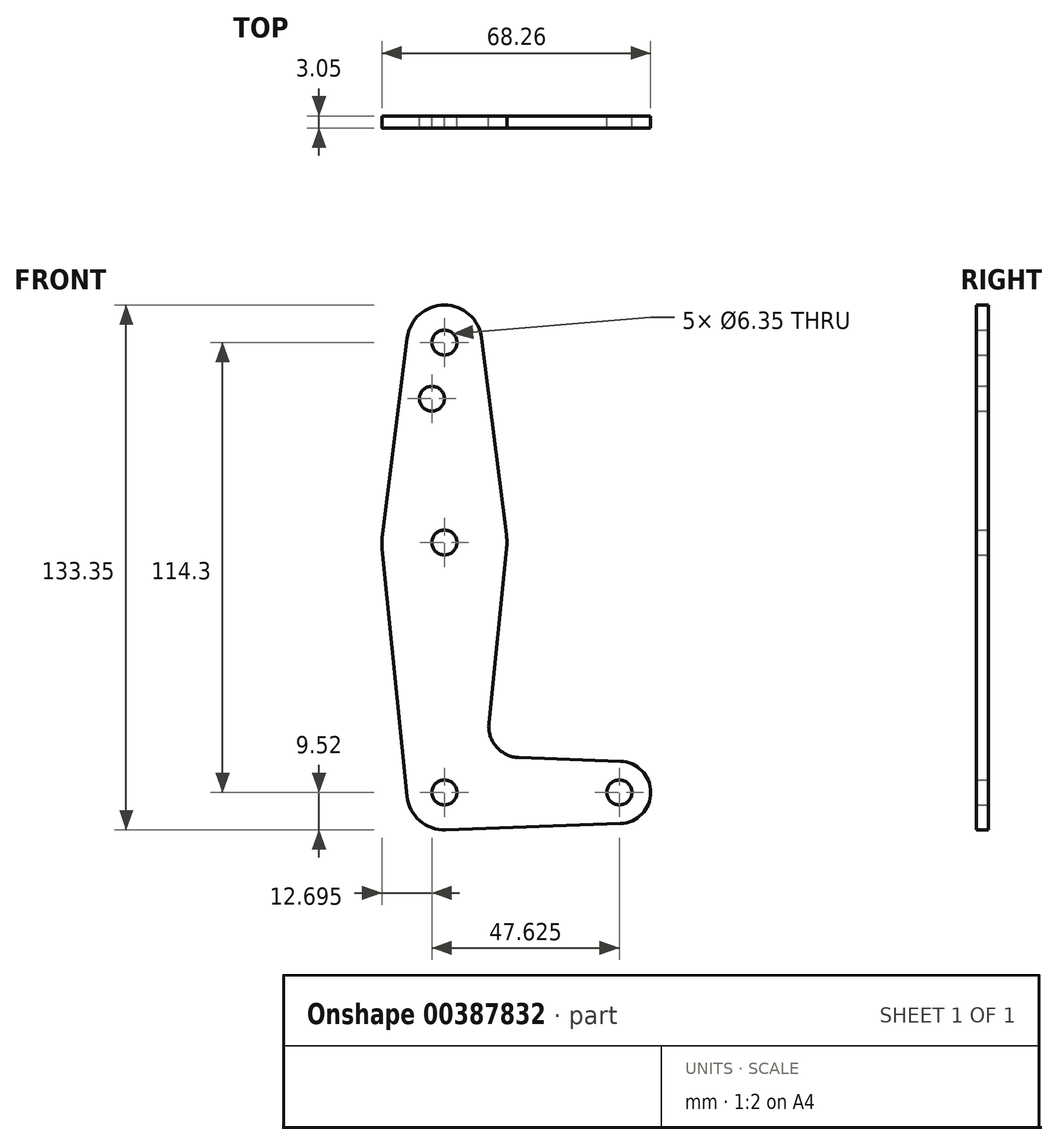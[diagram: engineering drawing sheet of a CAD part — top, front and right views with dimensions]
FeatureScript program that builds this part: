
annotation { "Feature Type Name" : "Feature", "Feature Type Description" : "" }
export const myFeature = defineFeature(function(context is Context, id is Id, definition is map)
    precondition{}
    {
        {
            var Q0;
            Q0=qCreatedBy(makeId("Front.planeOp"),FACE);
            var sketch = newSketch(context, id + "F0", { "sketchPlane" : qUnion([Q0])});
            skLineSegment(sketch, "E0", {"start": v(0, 114.3) * mm, "end": v(0, 0) * mm, "construction": true});
            skLineSegment(sketch, "E1", {"start": v(0, 0) * mm, "end": v(44.45, 0) * mm, "construction": true});
            skCircle(sketch, "E2", {"center": v(0, 114.3) * mm, "radius": 9.53 * mm});
            skCircle(sketch, "E3", {"center": v(0, 63.5) * mm, "radius": 15.88 * mm});
            skCircle(sketch, "E4", {"center": v(44.45, 0) * mm, "radius": 7.94 * mm});
            skLineSegment(sketch, "E5", {"start": v(-9.45, 115.5) * mm, "end": v(-15.75, 65.48) * mm});
            skLineSegment(sketch, "E6", {"start": v(11.3, 17.6) * mm, "end": v(15.8, 61.9) * mm});
            skLineSegment(sketch, "E7", {"start": v(44.73, 7.93) * mm, "end": v(18.93, 8.85) * mm});
            skLineSegment(sketch, "E8", {"start": v(0, -9.53) * mm, "end": v(44.73, -7.93) * mm});
            skLineSegment(sketch, "E9", {"start": v(9.45, 115.5) * mm, "end": v(15.75, 65.48) * mm});
            skCircle(sketch, "E10", {"center": v(0, 114.3) * mm, "radius": 3.18 * mm});
            skCircle(sketch, "E11", {"center": v(-3.17, 100.03) * mm, "radius": 3.18 * mm});
            skArc(sketch, "E12.filletArc", {"start": v(11.3, 17.6) * mm, "mid": v(13.22, 11.57) * mm, "end": v(18.93, 8.85) * mm});
            skCircle(sketch, "E13", {"center": v(0, 0) * mm, "radius": 3.18 * mm});
            skCircle(sketch, "E14", {"center": v(0, 63.5) * mm, "radius": 3.18 * mm});
            skCircle(sketch, "E15", {"center": v(44.45, 0) * mm, "radius": 3.17 * mm});
            skCircle(sketch, "E16", {"center": v(0, 0) * mm, "radius": 9.52 * mm});
            skLineSegment(sketch, "E17", {"start": v(-15.8, 61.91) * mm, "end": v(-9.47, -0.95) * mm});
            skSolve(sketch);
        }
        {
            var Q0;
            Q0 = qSketchRegion(id + "F0", true);
            extrude(context, id + "F1", {"entities" : qUnion([Q0]), "depth" : 3.05 * mm});
        }
    });
